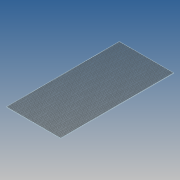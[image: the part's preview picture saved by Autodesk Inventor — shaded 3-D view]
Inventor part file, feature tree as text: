
AUTODESK INVENTOR PART (.ipt)
format: ipt  version: 2014 (Build 180170000, 170)  size: 79,872 bytes
history: native  units: mm
features: extrude x1, sketch x1
ambient origin geometry x8: Origin, YZ Plane, XZ Plane, XY Plane, X Axis, Y Axis, Z Axis, Center Point
bodies: Volumenkörper1 (feature_tree)
feature tree (2):
  extrude  "Extrusion1"  Depth=224.5mm
  sketch  "Skizze1"  dims[d0=108.0mm d1=224.5mm d2=0.8mm d3=0.0mm]
